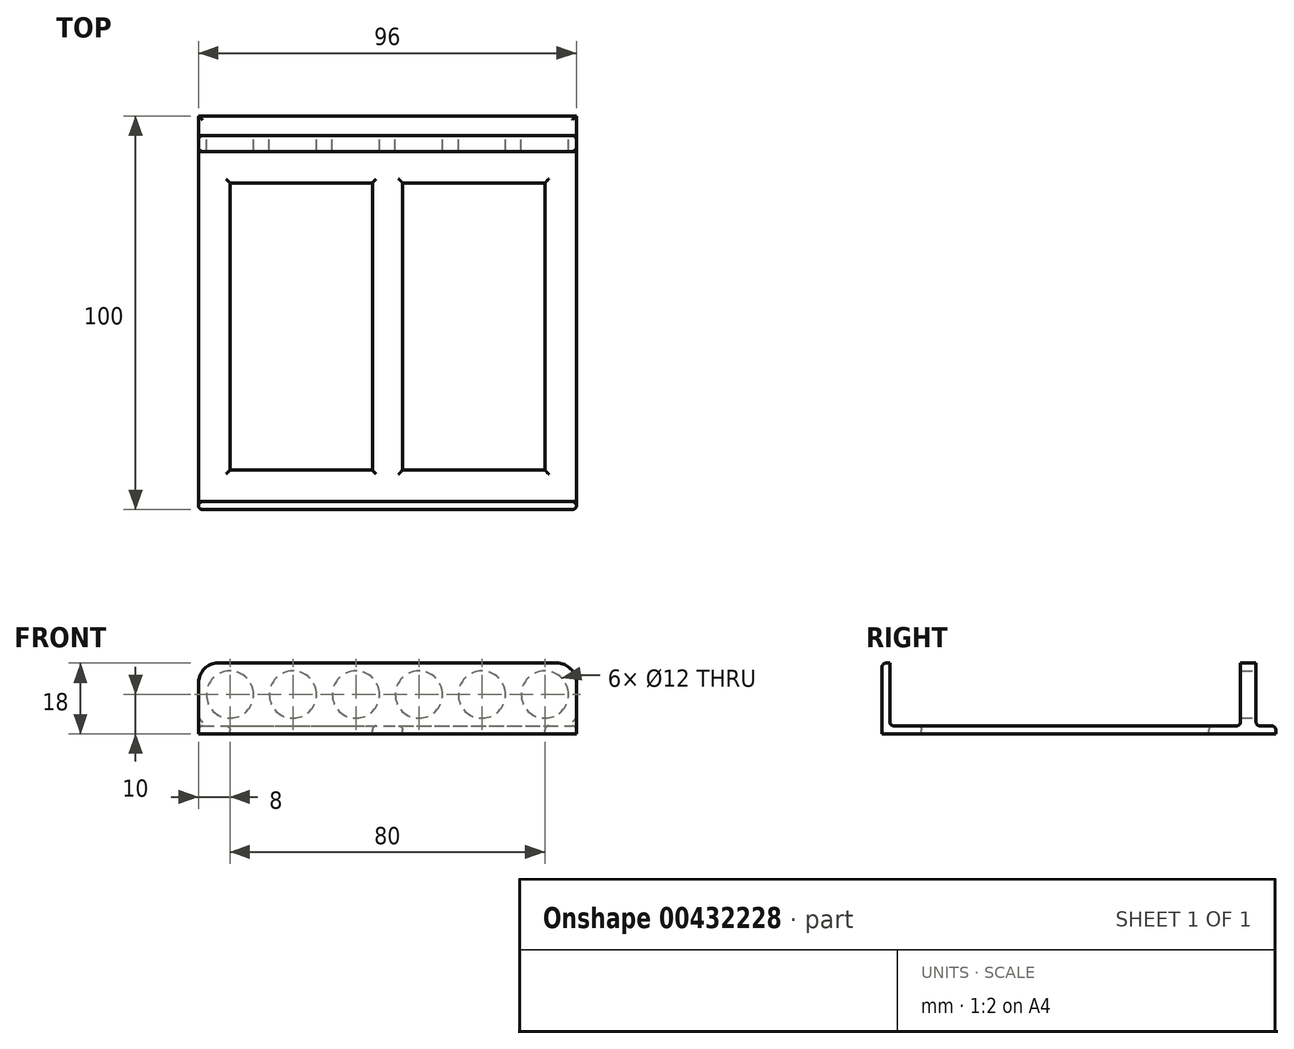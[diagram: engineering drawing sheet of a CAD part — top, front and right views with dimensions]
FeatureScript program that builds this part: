
annotation { "Feature Type Name" : "Feature", "Feature Type Description" : "" }
export const myFeature = defineFeature(function(context is Context, id is Id, definition is map)
    precondition{}
    {
        {
            var Q0;
            Q0=qCreatedBy(makeId("Top.planeOp"),FACE);
            var sketch = newSketch(context, id + "F0", { "sketchPlane" : qUnion([Q0])});
            skLineSegment(sketch, "E0.bottom", {"start": v(48, 50) * mm, "end": v(-48, 50) * mm});
            skLineSegment(sketch, "E0.top", {"start": v(48, -50) * mm, "end": v(-48, -50) * mm});
            skLineSegment(sketch, "E0.left", {"start": v(48, 50) * mm, "end": v(48, -50) * mm});
            skLineSegment(sketch, "E0.right", {"start": v(-48, 50) * mm, "end": v(-48, -50) * mm});
            skPoint(sketch, "E0.middle", {"position": v(0, 0) * mm});
            skSolve(sketch);
        }
        {
            var Q0;
            Q0 = qSketchRegion(id + "F0", true);
            extrude(context, id + "F1", {"entities" : qUnion([Q0]), "depth" : 2 * mm});
        }
        {
            var Q0;
            Q0=makeQuery(id+"F1.opExtrude","CAP_FACE",FACE,{"disambiguationData":[OSD([sQuery(id+"F0.wireOp",EDGE,"E0.bottom"),sQuery(id+"F0.wireOp",EDGE,"E0.top"),sQuery(id+"F0.wireOp",EDGE,"E0.left"),sQuery(id+"F0.wireOp",EDGE,"E0.right")])],"isStart":false});
            var sketch = newSketch(context, id + "F2", { "sketchPlane" : qUnion([Q0])});
            skLineSegment(sketch, "E1.bottom", {"start": v(-48, -50) * mm, "end": v(48, -50) * mm});
            skLineSegment(sketch, "E1.top", {"start": v(-48, -48) * mm, "end": v(48, -48) * mm});
            skLineSegment(sketch, "E1.left", {"start": v(-48, -50) * mm, "end": v(-48, -48) * mm});
            skLineSegment(sketch, "E1.right", {"start": v(48, -50) * mm, "end": v(48, -48) * mm});
            skSolve(sketch);
        }
        {
            var Q0;
            Q0 = qSketchRegion(id + "F2", true);
            extrude(context, id + "F3", {"entities" : qUnion([Q0]), "operationType" : NewBodyOperationType.ADD, "depth" : 16 * mm});
        }
        {
            var Q0;
            Q0=makeQuery(id+"F1.opExtrude","CAP_FACE",FACE,{"disambiguationData":[OSD([sQuery(id+"F0.wireOp",EDGE,"E0.bottom"),sQuery(id+"F0.wireOp",EDGE,"E0.top"),sQuery(id+"F0.wireOp",EDGE,"E0.left"),sQuery(id+"F0.wireOp",EDGE,"E0.right")])],"isStart":false});
            var sketch = newSketch(context, id + "F4", { "sketchPlane" : qUnion([Q0])});
            skLineSegment(sketch, "E2.bottom", {"start": v(-48, 45) * mm, "end": v(48, 45) * mm});
            skLineSegment(sketch, "E2.top", {"start": v(-48, 41) * mm, "end": v(48, 41) * mm});
            skLineSegment(sketch, "E2.left", {"start": v(-48, 45) * mm, "end": v(-48, 41) * mm});
            skLineSegment(sketch, "E2.right", {"start": v(48, 45) * mm, "end": v(48, 41) * mm});
            skSolve(sketch);
        }
        {
            var Q0;
            Q0 = qSketchRegion(id + "F4", true);
            extrude(context, id + "F5", {"entities" : qUnion([Q0]), "operationType" : NewBodyOperationType.ADD, "depth" : 16 * mm});
        }
        {
            var Q0;
            Q0=makeQuery(id+"F5.opExtrude","CAP_EDGE",EDGE,{"disambiguationData":[OSD([sQuery(id+"F4.wireOp",EDGE,"E2.left")])],"isStart":false});
            var Q1;
            Q1=makeQuery(id+"F5.opExtrude","CAP_EDGE",EDGE,{"disambiguationData":[OSD([sQuery(id+"F4.wireOp",EDGE,"E2.right")])],"isStart":false});
            var Q2;
            Q2=makeQuery(id+"F3.opExtrude","CAP_EDGE",EDGE,{"disambiguationData":[OSD([sQuery(id+"F2.wireOp",EDGE,"E1.right")])],"isStart":false});
            var Q3;
            Q3=makeQuery(id+"F3.opExtrude","CAP_EDGE",EDGE,{"disambiguationData":[OSD([sQuery(id+"F2.wireOp",EDGE,"E1.left")])],"isStart":false});
            fillet(context, id + "F6", {"entities" : qUnion([Q0, Q1, Q2, Q3]), "radius" : 5 * mm, "tangentPropagation" : true, "allowEdgeOverflow" : false});
        }
        {
            var Q0;
            Q0=makeQuery(id+"F5.opExtrude","SWEPT_FACE",FACE,{"disambiguationData":[OSD([sQuery(id+"F4.wireOp",EDGE,"E2.bottom")])]});
            var sketch = newSketch(context, id + "F7", { "sketchPlane" : qUnion([Q0])});
            skCircle(sketch, "E3", {"center": v(-40, 10) * mm, "radius": 6 * mm});
            skCircle(sketch, "E4.1.0.0", {"center": v(-24, 10) * mm, "radius": 6 * mm});
            skCircle(sketch, "E4.2.0.0", {"center": v(-8, 10) * mm, "radius": 6 * mm});
            skCircle(sketch, "E4.3.0.0", {"center": v(8, 10) * mm, "radius": 6 * mm});
            skCircle(sketch, "E4.4.0.0", {"center": v(24, 10) * mm, "radius": 6 * mm});
            skCircle(sketch, "E4.5.0.0", {"center": v(40, 10) * mm, "radius": 6 * mm});
            skLineSegment(sketch, "E4.direction1", {"start": v(-40, 10) * mm, "end": v(-24, 10) * mm, "construction": true});
            skSolve(sketch);
        }
        {
            var Q0;
            Q0 = qSketchRegion(id + "F7", true);
            extrude(context, id + "F8", {"entities" : qUnion([Q0]), "operationType" : NewBodyOperationType.REMOVE, "endBound" : BoundingType.UP_TO_NEXT, "oppositeDirection" : true, "depth" : 25 * mm});
        }
        {
            var Q0;
            {var subQ0=sQuery(id+"F0.wireOp",EDGE,"E0.right");var subQ1=sQuery(id+"F0.wireOp",EDGE,"E0.left");Q0=makeQuery(id+"F5.boolean.opBoolean","SPLIT",FACE,{"disambiguationData":[TD([makeQuery(id+"F3.opExtrude","SWEPT_FACE",FACE,{"disambiguationData":[OSD([sQuery(id+"F2.wireOp",EDGE,"E1.top")])]})])],"derivedFrom":makeQuery(id+"F1.opExtrude","CAP_FACE",FACE,{"disambiguationData":[OSD([sQuery(id+"F0.wireOp",EDGE,"E0.bottom"),sQuery(id+"F0.wireOp",EDGE,"E0.top"),subQ1,subQ0])],"isStart":false})});}
            var Q1;
            {var subQ0=sQuery(id+"F0.wireOp",EDGE,"E0.right");var subQ1=sQuery(id+"F0.wireOp",EDGE,"E0.left");var subQ2=sQuery(id+"F0.wireOp",EDGE,"E0.bottom");Q1=makeQuery(id+"F5.boolean.opBoolean","SPLIT",FACE,{"disambiguationData":[TD([makeQuery(id+"F1.opExtrude","SWEPT_FACE",FACE,{"disambiguationData":[OSD([subQ2])]})])],"derivedFrom":makeQuery(id+"F1.opExtrude","CAP_FACE",FACE,{"disambiguationData":[OSD([subQ2,sQuery(id+"F0.wireOp",EDGE,"E0.top"),subQ1,subQ0])],"isStart":false})});}
            var Q2;
            Q2=makeQuery(id+"F3.opExtrude","CAP_EDGE",EDGE,{"disambiguationData":[OSD([sQuery(id+"F2.wireOp",EDGE,"E1.bottom")])],"isStart":false});
            fillet(context, id + "F9", {"entities" : qUnion([Q0, Q1, Q2]), "radius" : 1 * mm, "tangentPropagation" : true, "allowEdgeOverflow" : false});
        }
        {
            var Q0;
            {var subQ0=sQuery(id+"F0.wireOp",EDGE,"E0.right");var subQ1=sQuery(id+"F0.wireOp",EDGE,"E0.left");Q0=makeQuery(id+"F5.boolean.opBoolean","SPLIT",FACE,{"disambiguationData":[TD([makeQuery(id+"F3.opExtrude","SWEPT_FACE",FACE,{"disambiguationData":[OSD([sQuery(id+"F2.wireOp",EDGE,"E1.top")])]})])],"derivedFrom":makeQuery(id+"F1.opExtrude","CAP_FACE",FACE,{"disambiguationData":[OSD([sQuery(id+"F0.wireOp",EDGE,"E0.bottom"),sQuery(id+"F0.wireOp",EDGE,"E0.top"),subQ1,subQ0])],"isStart":false})});}
            var sketch = newSketch(context, id + "F10", { "sketchPlane" : qUnion([Q0])});
            skLineSegment(sketch, "E5.bottom", {"start": v(-40, 33) * mm, "end": v(-3.83, 33) * mm});
            skLineSegment(sketch, "E5.top", {"start": v(-40, -40) * mm, "end": v(-3.83, -40) * mm});
            skLineSegment(sketch, "E5.left", {"start": v(-40, 33) * mm, "end": v(-40, -40) * mm});
            skLineSegment(sketch, "E5.right", {"start": v(-3.83, 33) * mm, "end": v(-3.83, -40) * mm});
            skLineSegment(sketch, "E6.bottom", {"start": v(3.83, 33) * mm, "end": v(40, 33) * mm});
            skLineSegment(sketch, "E6.top", {"start": v(3.83, -40) * mm, "end": v(40, -40) * mm});
            skLineSegment(sketch, "E6.left", {"start": v(3.83, 33) * mm, "end": v(3.83, -40) * mm});
            skLineSegment(sketch, "E6.right", {"start": v(40, 33) * mm, "end": v(40, -40) * mm});
            skSolve(sketch);
        }
        {
            var Q0;
            Q0 = qSketchRegion(id + "F10", true);
            extrude(context, id + "F11", {"entities" : qUnion([Q0]), "operationType" : NewBodyOperationType.REMOVE, "endBound" : BoundingType.UP_TO_NEXT, "oppositeDirection" : true, "depth" : 25 * mm});
        }
        {
            var Q0;
            {var subQ0=sQuery(id+"F0.wireOp",EDGE,"E0.right");var subQ1=sQuery(id+"F0.wireOp",EDGE,"E0.left");Q0=makeQuery(id+"F5.boolean.opBoolean","SPLIT",FACE,{"disambiguationData":[TD([makeQuery(id+"F3.opExtrude","SWEPT_FACE",FACE,{"disambiguationData":[OSD([sQuery(id+"F2.wireOp",EDGE,"E1.top")])]})])],"derivedFrom":makeQuery(id+"F1.opExtrude","CAP_FACE",FACE,{"disambiguationData":[OSD([sQuery(id+"F0.wireOp",EDGE,"E0.bottom"),sQuery(id+"F0.wireOp",EDGE,"E0.top"),subQ1,subQ0])],"isStart":false})});}
            fillet(context, id + "F12", {"entities" : qUnion([Q0]), "radius" : 1 * mm, "tangentPropagation" : true, "allowEdgeOverflow" : false});
        }
    });
